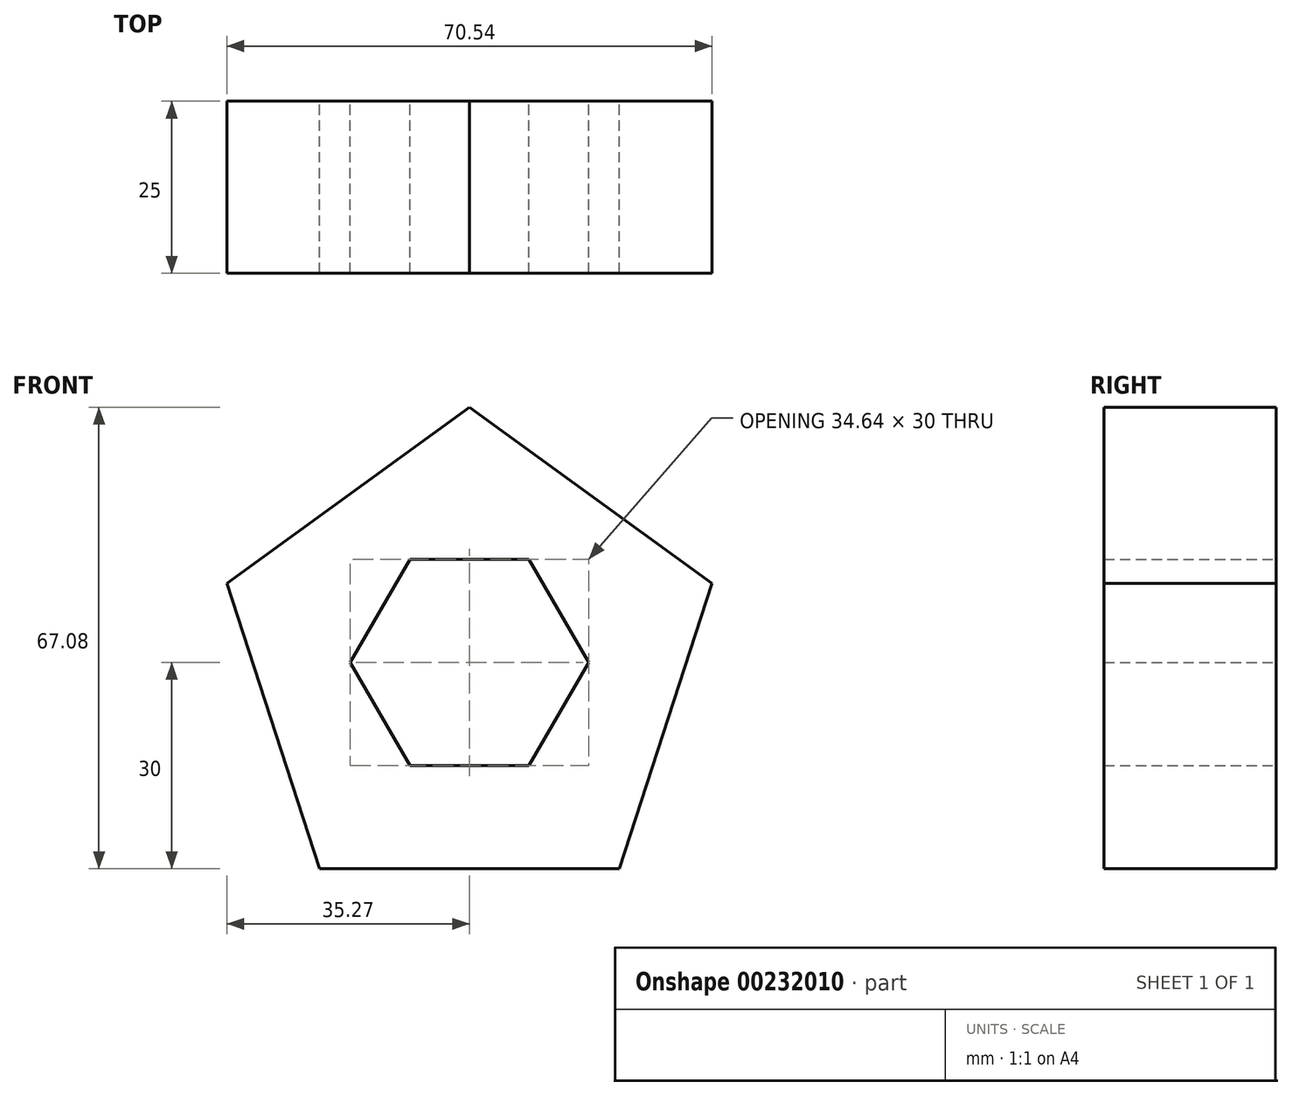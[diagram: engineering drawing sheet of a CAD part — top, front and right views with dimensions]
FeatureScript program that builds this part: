
annotation { "Feature Type Name" : "Feature", "Feature Type Description" : "" }
export const myFeature = defineFeature(function(context is Context, id is Id, definition is map)
    precondition{}
    {
        {
            var Q0;
            Q0=qCreatedBy(makeId("Front.planeOp"),FACE);
            var sketch = newSketch(context, id + "F0", { "sketchPlane" : qUnion([Q0])});
            skLineSegment(sketch, "E0.0", {"start": v(-8.66, 15) * mm, "end": v(8.66, 15) * mm});
            skLineSegment(sketch, "E0.1", {"start": v(8.66, 15) * mm, "end": v(17.32, 0) * mm});
            skLineSegment(sketch, "E0.2", {"start": v(17.32, 0) * mm, "end": v(8.66, -15) * mm});
            skLineSegment(sketch, "E0.3", {"start": v(8.66, -15) * mm, "end": v(-8.66, -15) * mm});
            skLineSegment(sketch, "E0.4", {"start": v(-8.66, -15) * mm, "end": v(-17.32, 0) * mm});
            skLineSegment(sketch, "E0.5", {"start": v(-17.32, 0) * mm, "end": v(-8.66, 15) * mm});
            skPoint(sketch, "E0.0.midPoint", {"position": v(0, 15) * mm});
            skLineSegment(sketch, "E1.0", {"start": v(21.8, -30) * mm, "end": v(-21.8, -30) * mm});
            skLineSegment(sketch, "E1.1", {"start": v(-21.8, -30) * mm, "end": v(-35.27, 11.46) * mm});
            skLineSegment(sketch, "E1.2", {"start": v(-35.27, 11.46) * mm, "end": v(0, 37.08) * mm});
            skLineSegment(sketch, "E1.3", {"start": v(0, 37.08) * mm, "end": v(35.27, 11.46) * mm});
            skLineSegment(sketch, "E1.4", {"start": v(35.27, 11.46) * mm, "end": v(21.8, -30) * mm});
            skPoint(sketch, "E1.0.midPoint", {"position": v(0, -30) * mm});
            skSolve(sketch);
        }
        {
            var Q0;
            Q0=makeQuery(id+"F0.imprint","IMPRINT",FACE,{"disambiguationData":[TD([[makeQuery(id+"F0.imprint","IMPRINT",EDGE,{"derivedFrom":sQuery(id+"F0.wireOp",EDGE,"E0.0")}),1.0]])]});
            extrude(context, id + "F1", {"entities" : qUnion([Q0]), "depth" : 25 * mm});
        }
    });
